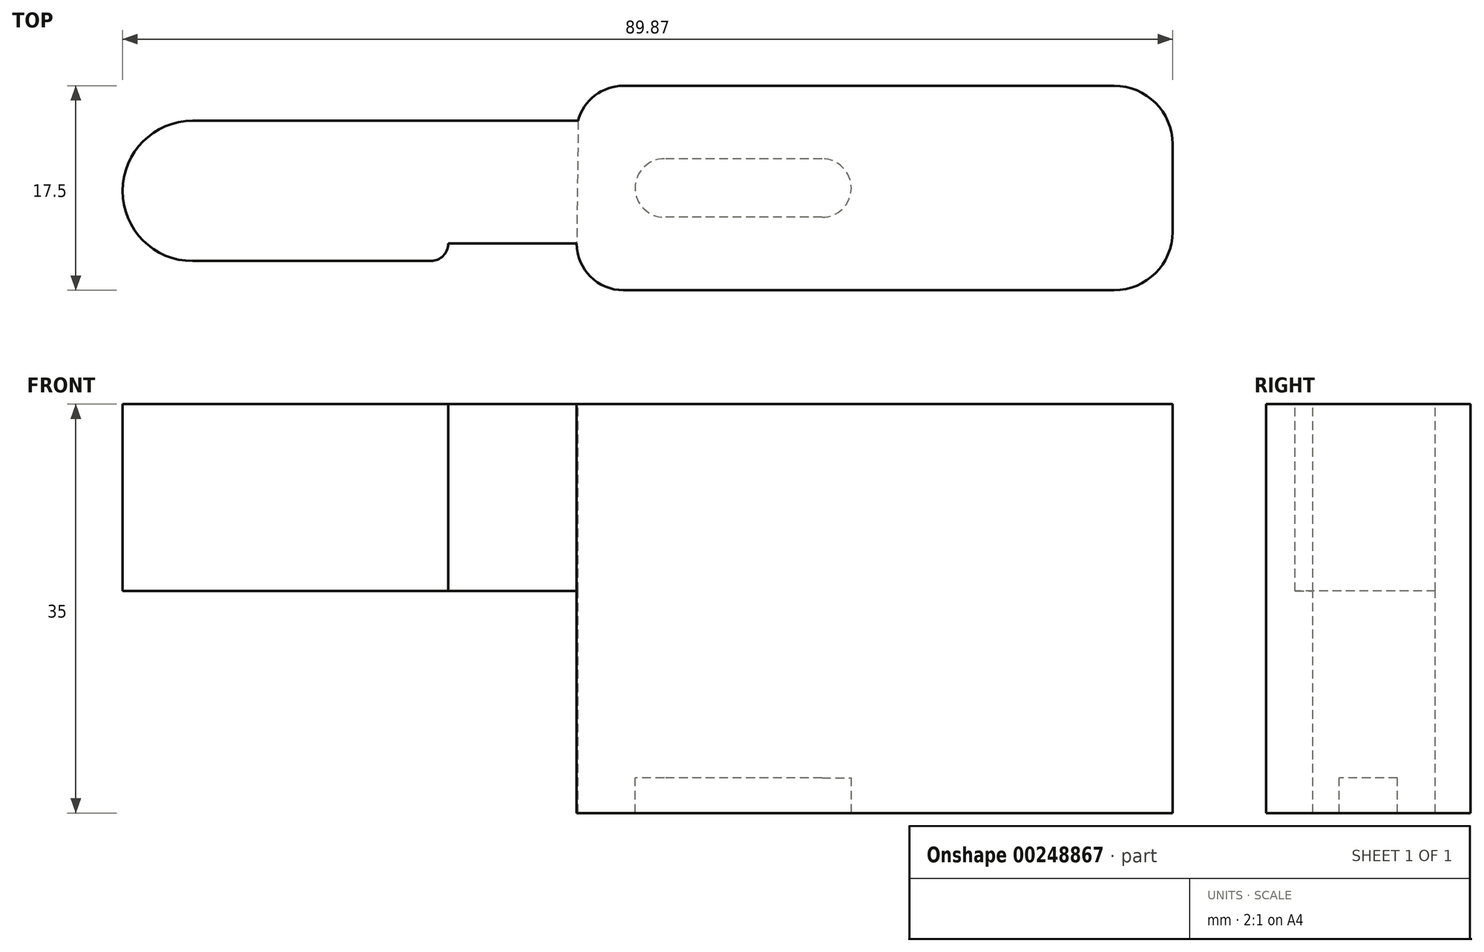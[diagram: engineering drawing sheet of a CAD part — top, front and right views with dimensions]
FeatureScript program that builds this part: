
annotation { "Feature Type Name" : "Feature", "Feature Type Description" : "" }
export const myFeature = defineFeature(function(context is Context, id is Id, definition is map)
    precondition{}
    {
        {
            var Q0;
            Q0=qCreatedBy(makeId("Top.planeOp"),FACE);
            var sketch = newSketch(context, id + "F0", { "sketchPlane" : qUnion([Q0])});
            skLineSegment(sketch, "E0.bottom", {"start": v(-20.5, 8.75) * mm, "end": v(21.5, 8.75) * mm});
            skLineSegment(sketch, "E0.top", {"start": v(-20.5, -8.75) * mm, "end": v(21.5, -8.75) * mm});
            skLineSegment(sketch, "E0.right", {"start": v(26.5, 3.75) * mm, "end": v(26.5, -3.75) * mm});
            skPoint(sketch, "E0.middle", {"position": v(0, 0) * mm});
            skPoint(sketch, "E1.visualSharp", {"position": v(26.5, 8.75) * mm});
            skArc(sketch, "E1.filletArc", {"start": v(26.5, 3.75) * mm, "mid": v(25.04, 7.29) * mm, "end": v(21.5, 8.75) * mm});
            skPoint(sketch, "E2.visualSharp", {"position": v(26.5, -8.75) * mm});
            skArc(sketch, "E2.filletArc", {"start": v(21.5, -8.75) * mm, "mid": v(25.04, -7.29) * mm, "end": v(26.5, -3.75) * mm});
            skPoint(sketch, "E3.newPointA", {"position": v(-26.5, 8.75) * mm});
            skArc(sketch, "E3.filletArc", {"start": v(-20.5, 8.75) * mm, "mid": v(-22.95, 7.91) * mm, "end": v(-24.37, 5.75) * mm});
            skPoint(sketch, "E4.visualSharp", {"position": v(-26.5, -8.75) * mm});
            skArc(sketch, "E4.filletArc", {"start": v(-24.5, -4.75) * mm, "mid": v(-23.33, -7.58) * mm, "end": v(-20.5, -8.75) * mm});
            skLineSegment(sketch, "E5", {"start": v(-24.37, 5.75) * mm, "end": v(-57.37, 5.75) * mm});
            skLineSegment(sketch, "E6", {"start": v(-24.5, -4.75) * mm, "end": v(-35.5, -4.75) * mm});
            skLineSegment(sketch, "E7", {"start": v(-35.5, -4.75) * mm, "end": v(-35.5, -4.75) * mm});
            skLineSegment(sketch, "E8", {"start": v(-37, -6.25) * mm, "end": v(-57.37, -6.25) * mm});
            skPoint(sketch, "E9.visualSharp", {"position": v(-35.5, -6.25) * mm});
            skArc(sketch, "E9.filletArc", {"start": v(-37, -6.25) * mm, "mid": v(-35.94, -5.81) * mm, "end": v(-35.5, -4.75) * mm});
            skArc(sketch, "E10", {"start": v(-57.37, 5.75) * mm, "mid": v(-63.37, -0.25) * mm, "end": v(-57.37, -6.25) * mm});
            skLineSegment(sketch, "E11", {"start": v(-24.37, 5.75) * mm, "end": v(-24.5, -4.75) * mm});
            skSolve(sketch);
        }
        {
            var Q0;
            {var subQ3=sQuery(id+"F0.wireOp",EDGE,"E0.bottom");Q0=makeQuery(id+"F0.imprint","IMPRINT",FACE,{"disambiguationData":[TD([[makeQuery(id+"F0.imprint","IMPRINT",EDGE,{"derivedFrom":subQ3}),-1.0]])]});}
            extrude(context, id + "F1", {"entities" : qUnion([Q0]), "oppositeDirection" : true, "depth" : 32 * mm});
        }
        {
            var Q0;
            Q0=makeQuery(id+"F0.imprint","IMPRINT",FACE,{"disambiguationData":[TD([[makeQuery(id+"F0.imprint","IMPRINT",EDGE,{"derivedFrom":sQuery(id+"F0.wireOp",EDGE,"E5")}),1.0]])]});
            extrude(context, id + "F2", {"entities" : qUnion([Q0]), "operationType" : NewBodyOperationType.ADD, "oppositeDirection" : true, "depth" : (16) * mm});
        }
        {
            var Q0;
            Q0=makeQuery(id+"F1.opExtrude","CAP_FACE",FACE,{"disambiguationData":[OSD([sQuery(id+"F0.wireOp",EDGE,"E0.bottom"),sQuery(id+"F0.wireOp",EDGE,"E0.top"),sQuery(id+"F0.wireOp",EDGE,"E0.right"),sQuery(id+"F0.wireOp",EDGE,"E1.filletArc"),sQuery(id+"F0.wireOp",EDGE,"E2.filletArc"),sQuery(id+"F0.wireOp",EDGE,"E3.filletArc"),sQuery(id+"F0.wireOp",EDGE,"E4.filletArc"),sQuery(id+"F0.wireOp",EDGE,"E11")])],"isStart":false});
            var sketch = newSketch(context, id + "F3", { "sketchPlane" : qUnion([Q0])});
            skLineSegment(sketch, "E12", {"start": v(-3.5, 0) * mm, "end": v(-17, 0) * mm});
            skArc(sketch, "E13.0.startCap", {"start": v(-3.5, 2.5) * mm, "mid": v(-1, 0) * mm, "end": v(-3.5, -2.5) * mm});
            skArc(sketch, "E13.0.endCap", {"start": v(-17, -2.5) * mm, "mid": v(-19.5, 0) * mm, "end": v(-17, 2.5) * mm});
            skLineSegment(sketch, "E13.0.left", {"start": v(-3.5, -2.5) * mm, "end": v(-17, -2.5) * mm});
            skLineSegment(sketch, "E13.0.right", {"start": v(-3.5, 2.5) * mm, "end": v(-17, 2.5) * mm});
            skSolve(sketch);
        }
        {
            var Q0;
            Q0=makeQuery(id+"F3.imprint","IMPRINT",FACE,{"disambiguationData":[TD([[makeQuery(id+"F3.imprint","IMPRINT",EDGE,{"derivedFrom":sQuery(id+"F3.wireOp",EDGE,"E13.0.startCap")}),-1.0]])]});
            extrude(context, id + "F4", {"entities" : qUnion([Q0]), "operationType" : NewBodyOperationType.ADD, "depth" : 3 * mm});
        }
    });
